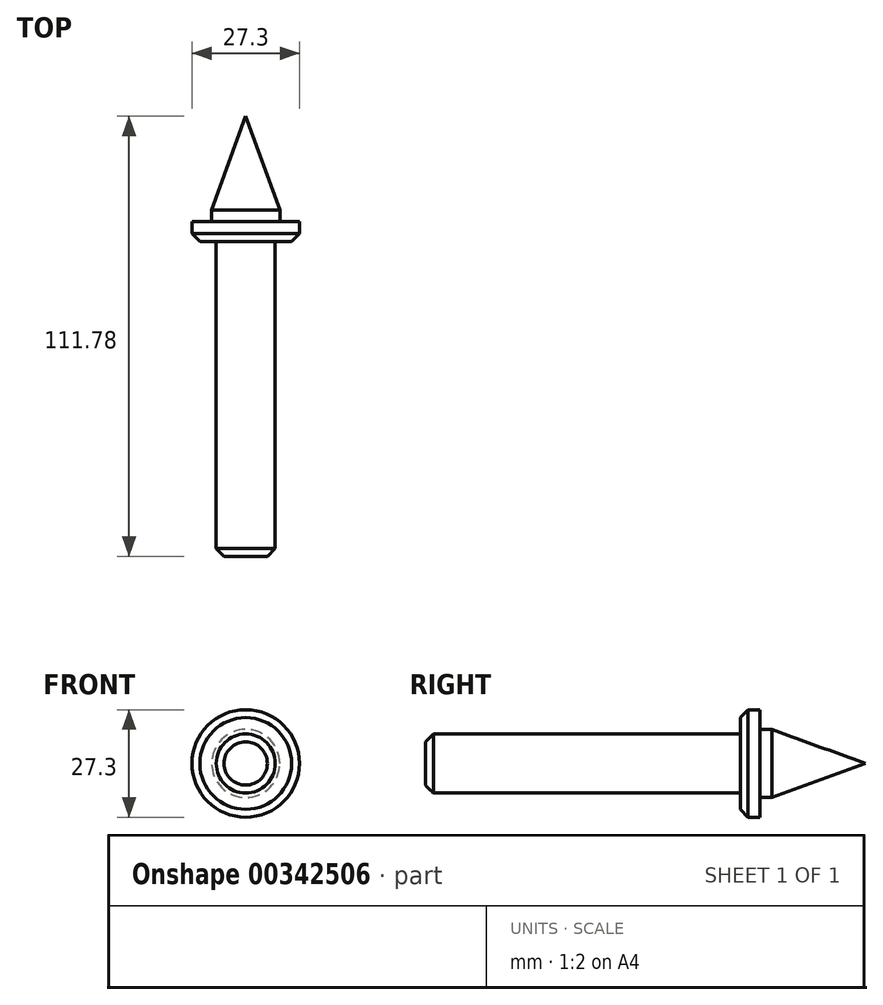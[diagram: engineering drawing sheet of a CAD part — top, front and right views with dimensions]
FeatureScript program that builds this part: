
annotation { "Feature Type Name" : "Feature", "Feature Type Description" : "" }
export const myFeature = defineFeature(function(context is Context, id is Id, definition is map)
    precondition{}
    {
        {
            var Q0;
            Q0=qCreatedBy(makeId("Front.planeOp"),FACE);
            var sketch = newSketch(context, id + "F0", { "sketchPlane" : qUnion([Q0])});
            skCircle(sketch, "E0", {"center": v(0, 0) * mm, "radius": 7.5 * mm});
            skSolve(sketch);
        }
        {
            var Q0;
            Q0=makeQuery(id+"F0.imprint","IMPRINT",FACE,{"disambiguationData":[TD([[makeQuery(id+"F0.imprint","IMPRINT",EDGE,{"derivedFrom":sQuery(id+"F0.wireOp",EDGE,"E0")}),1.0]])]});
            var Q1;
            Q1=sQuery(id+"F0.wireOp",EDGE,"E0");
            extrude(context, id + "F1", {"entities" : qUnion([Q0]), "surfaceEntities" : qUnion([Q1]), "oppositeDirection" : true, "depth" : 80 * mm});
        }
        {
            var Q0;
            Q0=makeQuery(id+"F1.opExtrude","CAP_FACE",FACE,{"disambiguationData":[OSD([sQuery(id+"F0.wireOp",EDGE,"E0")])],"isStart":false});
            var sketch = newSketch(context, id + "F2", { "sketchPlane" : qUnion([Q0])});
            skCircle(sketch, "E1", {"center": v(0, 0) * mm, "radius": 13.65 * mm});
            skSolve(sketch);
        }
        {
            var Q0;
            Q0 = qSketchRegion(id + "F2", true);
            extrude(context, id + "F3", {"entities" : qUnion([Q0]), "operationType" : NewBodyOperationType.ADD, "depth" : 5 * mm});
        }
        {
            var Q0;
            Q0=makeQuery(id+"F3.opExtrude","CAP_FACE",FACE,{"disambiguationData":[OSD([sQuery(id+"F2.wireOp",EDGE,"E1")])],"isStart":false});
            var sketch = newSketch(context, id + "F4", { "sketchPlane" : qUnion([Q0])});
            skCircle(sketch, "E2.0", {"center": v(0, 0) * mm, "radius": 8.65 * mm});
            skSolve(sketch);
        }
        {
            var Q0;
            Q0 = qSketchRegion(id + "F4", true);
            extrude(context, id + "F5", {"entities" : qUnion([Q0]), "operationType" : NewBodyOperationType.ADD, "depth" : 3 * mm});
        }
        {
            var Q0;
            Q0=makeQuery(id+"F5.opExtrude","CAP_FACE",FACE,{"disambiguationData":[OSD([sQuery(id+"F4.wireOp",EDGE,"E2.0")])],"isStart":false});
            extrude(context, id + "F6", {"entities" : qUnion([Q0]), "operationType" : NewBodyOperationType.ADD, "depth" : 25 * mm, "hasDraft" : true, "draftAngle" : 20 * degree, "draftPullDirection" : true});
        }
        {
            var Q0;
            Q0=makeQuery(id+"F1.opExtrude","CAP_EDGE",EDGE,{"disambiguationData":[OSD([sQuery(id+"F0.wireOp",EDGE,"E0")])],"isStart":true});
            var Q1;
            Q1=makeQuery(id+"F3.opExtrude","CAP_EDGE",EDGE,{"disambiguationData":[OSD([sQuery(id+"F2.wireOp",EDGE,"E1")])],"isStart":true});
            chamfer(context, id + "F7", {"entities" : qUnion([Q0, Q1]), "width" : 2 * mm, "tangentPropagation" : true});
        }
    });
